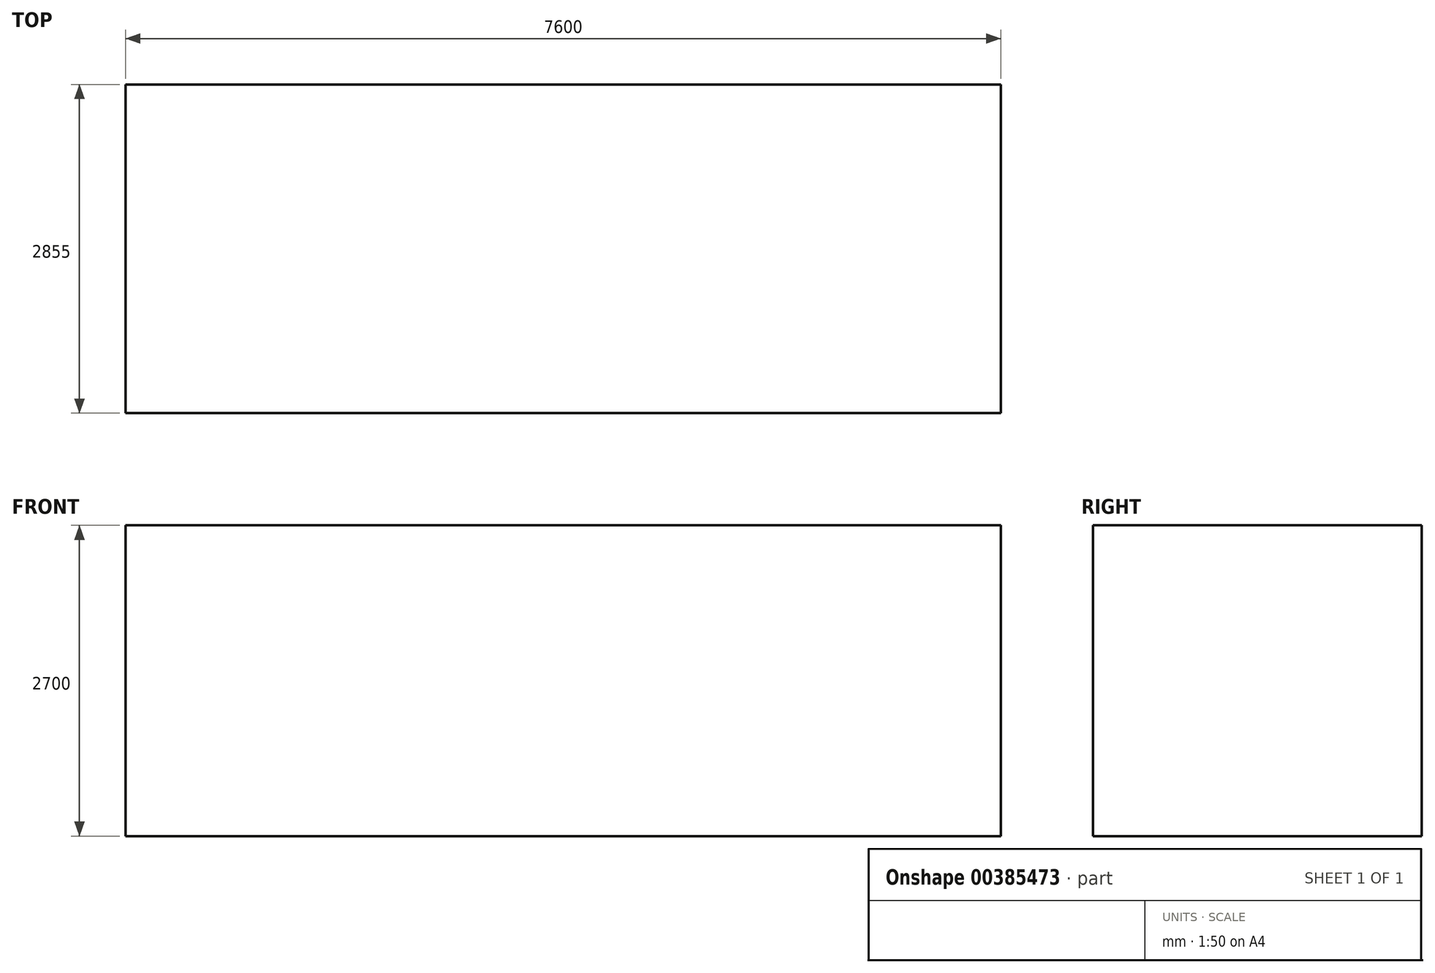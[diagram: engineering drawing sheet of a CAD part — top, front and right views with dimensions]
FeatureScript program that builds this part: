
annotation { "Feature Type Name" : "Feature", "Feature Type Description" : "" }
export const myFeature = defineFeature(function(context is Context, id is Id, definition is map)
    precondition{}
    {
        {
            var Q0;
            Q0=qCreatedBy(makeId("Top.planeOp"),FACE);
            var sketch = newSketch(context, id + "F0", { "sketchPlane" : qUnion([Q0])});
            skLineSegment(sketch, "E0.bottom", {"start": v(-3800, -1427.5) * mm, "end": v(3800, -1427.5) * mm});
            skLineSegment(sketch, "E0.top", {"start": v(-3800, 1427.5) * mm, "end": v(3800, 1427.5) * mm});
            skLineSegment(sketch, "E0.left", {"start": v(-3800, -1427.5) * mm, "end": v(-3800, 1427.5) * mm});
            skLineSegment(sketch, "E0.right", {"start": v(3800, -1427.5) * mm, "end": v(3800, 1427.5) * mm});
            skPoint(sketch, "E0.middle", {"position": v(0, 0) * mm});
            skSolve(sketch);
        }
        {
            var Q0;
            Q0=makeQuery(id+"F0.imprint","IMPRINT",FACE,{"disambiguationData":[TD([[makeQuery(id+"F0.imprint","IMPRINT",EDGE,{"derivedFrom":sQuery(id+"F0.wireOp",EDGE,"E0.bottom")}),1.0]])]});
            extrude(context, id + "F1", {"entities" : qUnion([Q0]), "depth" : 2700 * mm});
        }
    });
